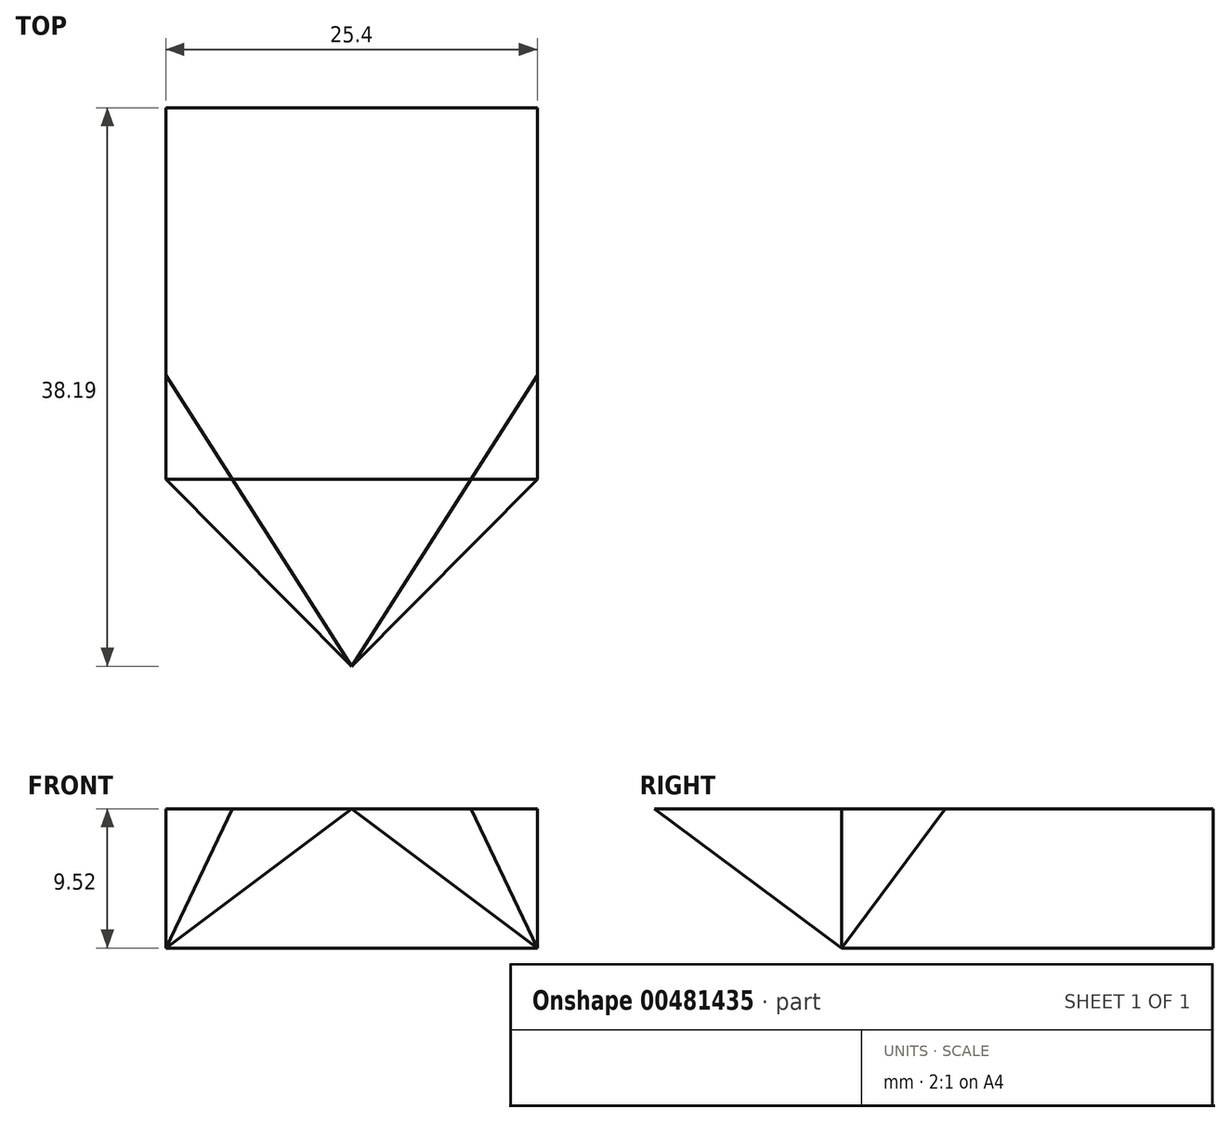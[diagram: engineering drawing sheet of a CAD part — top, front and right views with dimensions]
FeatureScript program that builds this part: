
annotation { "Feature Type Name" : "Feature", "Feature Type Description" : "" }
export const myFeature = defineFeature(function(context is Context, id is Id, definition is map)
    precondition{}
    {
        {
            var Q0;
            Q0=qCreatedBy(makeId("Front.planeOp"),FACE);
            var sketch = newSketch(context, id + "F0", { "sketchPlane" : qUnion([Q0])});
            skLineSegment(sketch, "E0.bottom", {"start": v(-12.7, -4.76) * mm, "end": v(12.7, -4.76) * mm});
            skLineSegment(sketch, "E0.top", {"start": v(-12.7, 4.76) * mm, "end": v(12.7, 4.76) * mm});
            skLineSegment(sketch, "E0.left", {"start": v(-12.7, -4.76) * mm, "end": v(-12.7, 4.76) * mm});
            skLineSegment(sketch, "E0.right", {"start": v(12.7, -4.76) * mm, "end": v(12.7, 4.76) * mm});
            skPoint(sketch, "E0.middle", {"position": v(0, 0) * mm});
            skSolve(sketch);
        }
        {
            var Q0;
            Q0 = qSketchRegion(id + "F0", true);
            extrude(context, id + "F1", {"entities" : qUnion([Q0]), "oppositeDirection" : true, "depth" : 25.4 * mm});
        }
        {
            var Q0;
            Q0=makeQuery(id+"F1.opExtrude","SWEPT_FACE",FACE,{"disambiguationData":[OSD([sQuery(id+"F0.wireOp",EDGE,"E0.right")])]});
            var sketch = newSketch(context, id + "F2", { "sketchPlane" : qUnion([Q0])});
            skLineSegment(sketch, "E1", {"start": v(0, 4.76) * mm, "end": v(-12.79, 4.76) * mm});
            skLineSegment(sketch, "E2", {"start": v(-12.79, 4.76) * mm, "end": v(0, -4.76) * mm});
            skSolve(sketch);
        }
        {
            var Q0;
            Q0=makeQuery(id+"F2.imprint","IMPRINT",FACE,{"disambiguationData":[TD([[makeQuery(id+"F2.imprint","IMPRINT",EDGE,{"derivedFrom":sQuery(id+"F2.wireOp",EDGE,"E1")}),1.0]])]});
            extrude(context, id + "F3", {"entities" : qUnion([Q0]), "oppositeDirection" : true, "depth" : 25.4 * mm});
        }
        {
            var Q0;
            Q0=makeQuery(id+"F3.opExtrude","SWEPT_FACE",FACE,{"disambiguationData":[OSD([sQuery(id+"F2.wireOp",EDGE,"E2")])]});
            var sketch = newSketch(context, id + "F4", { "sketchPlane" : qUnion([Q0])});
            skLineSegment(sketch, "E3", {"start": v(12.7, -2.84) * mm, "end": v(0, 13.1) * mm});
            skLineSegment(sketch, "E4", {"start": v(0, 13.1) * mm, "end": v(-12.7, -2.84) * mm});
            skLineSegment(sketch, "E5", {"start": v(-12.7, -2.84) * mm, "end": v(12.7, -2.84) * mm});
            skSolve(sketch);
        }
        {
            var Q0;
            {var subQ0=sQuery(id+"F4.wireOp",EDGE,"E4");Q0=makeQuery(id+"F4.imprint","IMPRINT",FACE,{"disambiguationData":[TD([[makeQuery(id+"F4.imprint","IMPRINT",EDGE,{"derivedFrom":subQ0}),-1.0]])]});}
            var Q1;
            {var subQ0=sQuery(id+"F4.wireOp",EDGE,"E3");Q1=makeQuery(id+"F4.imprint","IMPRINT",FACE,{"disambiguationData":[TD([[makeQuery(id+"F4.imprint","IMPRINT",EDGE,{"derivedFrom":subQ0}),-1.0]])]});}
            extrude(context, id + "F5", {"entities" : qUnion([Q0, Q1]), "operationType" : NewBodyOperationType.REMOVE, "oppositeDirection" : true, "depth" : 33.95 * mm});
        }
    });
